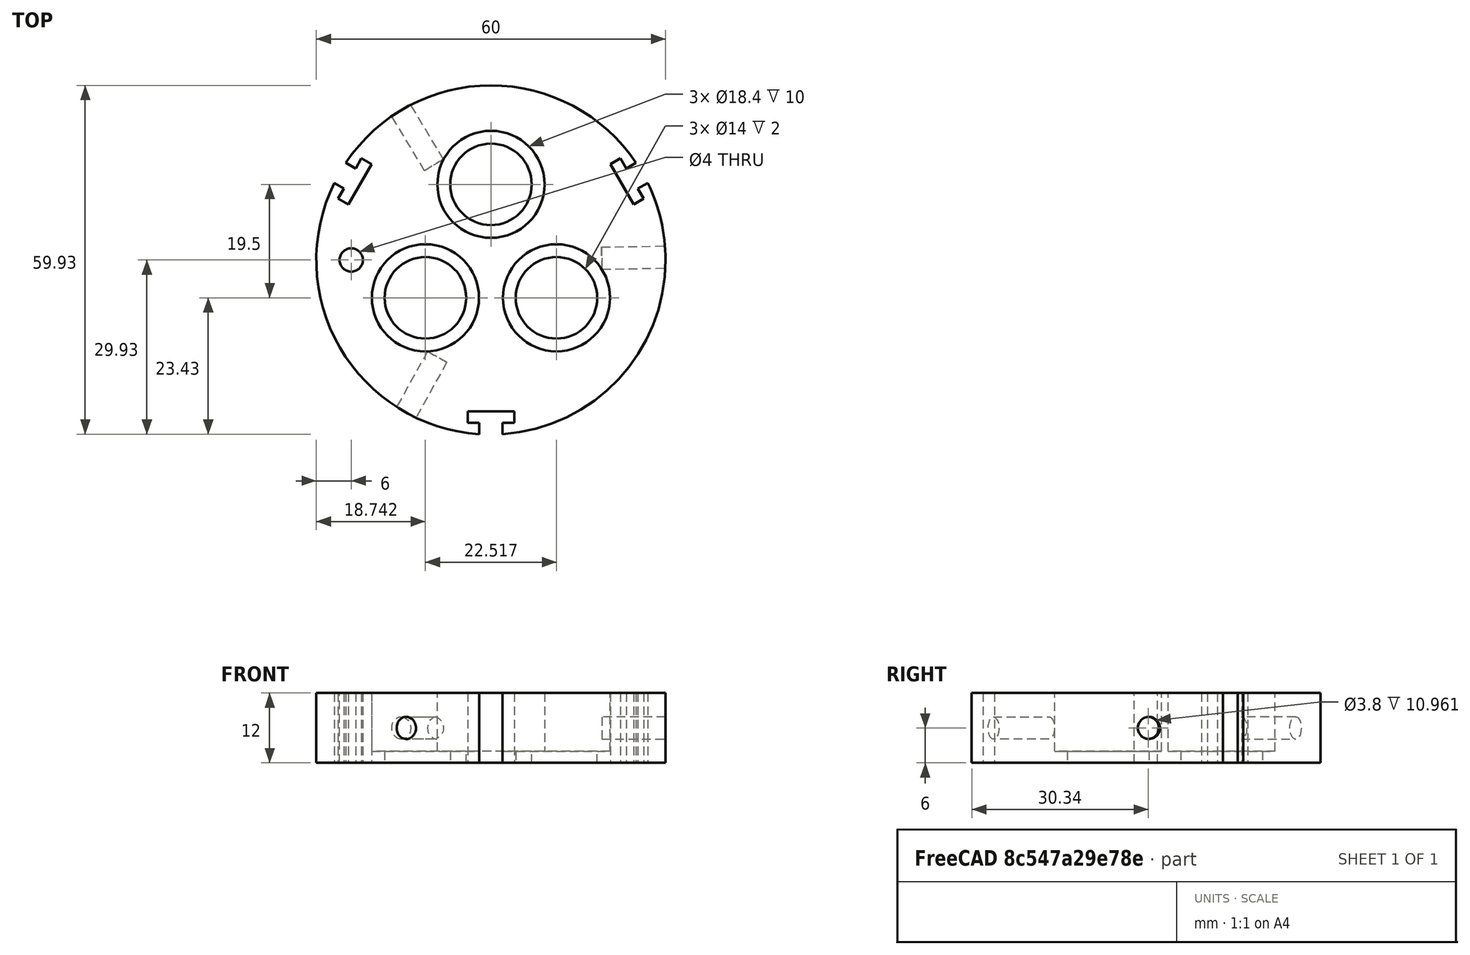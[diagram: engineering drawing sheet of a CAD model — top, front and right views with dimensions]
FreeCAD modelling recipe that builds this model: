
FCSTD DOCUMENT  (FreeCAD 1.0R38641 +468 (Git))
Label: Support_mot_3aileronsT_haut_60
License: All rights reserved
LicenseURL: https://en.wikipedia.org/wiki/All_rights_reserved
objects: Sketcher::SketchObject×6, PartDesign::Pocket×4, PartDesign::PolarPattern×3, PartDesign::Pad×2, PartDesign::Plane×1, PartDesign::Body×1, Mesh::Feature×1
note: 38 computed .brp shape members not serialized (recipe doc carries the construction recipe); baked Part::Feature solids carry a one-line shape summary decoded from their .brp

FEATURE [Sketcher::SketchObject] Sketch
  ArcFitTolerance = 1e-06
  AttachmentSupport = -> [XY_Plane]
  FullyConstrained = true
  MakeInternals = false
  MapMode = 5
  sketch-geometry (1):
    g0: Circle CenterX=0 CenterY=0 CenterZ=0 NormalX=0 NormalY=0 NormalZ=1 AngleXU=0 Radius=30
  constraints (2):
    c: Diameter(g0) = 60
    c: Coincident(g0,g-1)
FEATURE [PartDesign::Pad] Pad
  Direction = (0,0,1)
  Length = 12
  Length2 = 10
  Profile = -> Sketch
  ReferenceAxis = -> Sketch [N_Axis]
  Refine = true
  Suppressed = false
  Type = 0
FEATURE [Sketcher::SketchObject] Sketch001
  ArcFitTolerance = 1e-06
  AttachmentSupport = -> [Pad]
  FullyConstrained = true
  MakeInternals = false
  MapMode = 5
  Placement = pos=(0,0,12) rot=(0,0,1;0rad)
  sketch-geometry (1):
    g0: Circle CenterX=0 CenterY=13 CenterZ=0 NormalX=0 NormalY=0 NormalZ=1 AngleXU=0 Radius=9.2
  constraints (3):
    c: Diameter(g0) = 18.4
    c: PointOnObject(g0,g-2)
    c: DistanceY(g-1,g0) = 13
FEATURE [PartDesign::Pocket] Pocket
  BaseFeature = -> Pad
  Direction = (0,0,-1)
  Length = 5
  Length2 = 5
  Profile = -> Sketch001
  ReferenceAxis = -> Sketch001 [N_Axis]
  Refine = true
  Suppressed = false
  Type = 1
FEATURE [PartDesign::PolarPattern] PolarPattern
  Angle = 360
  Axis = -> Sketch001 [N_Axis]
  BaseFeature = -> Pocket
  Mode = 0
  Occurrences = 3
  Offset = 120
  Originals = -> [Pocket]
  Refine = true
  Suppressed = false
  TransformMode = 0
FEATURE [Sketcher::SketchObject] Sketch003
  ArcFitTolerance = 1e-06
  FullyConstrained = true
  MakeInternals = false
  MapMode = 5
  Placement = pos=(0,0,12) rot=(0,0,1;0rad)
  sketch-geometry (8):
    g0: LineSegment StartX=-2 StartY=-28 StartZ=0 EndX=-2 EndY=-32 EndZ=0
    g1: LineSegment StartX=-2 StartY=-32 StartZ=0 EndX=2 EndY=-32 EndZ=0
    g2: LineSegment StartX=2 StartY=-32 StartZ=0 EndX=2 EndY=-28 EndZ=0
    g3: LineSegment StartX=2 StartY=-28 StartZ=0 EndX=-2 EndY=-28 EndZ=0
    g4: LineSegment StartX=-4 StartY=-26 StartZ=0 EndX=-4 EndY=-28 EndZ=0
    g5: LineSegment StartX=-4 StartY=-28 StartZ=0 EndX=4 EndY=-28 EndZ=0
    g6: LineSegment StartX=4 StartY=-28 StartZ=0 EndX=4 EndY=-26 EndZ=0
    g7: LineSegment StartX=4 StartY=-26 StartZ=0 EndX=-4 EndY=-26 EndZ=0
  constraints (24):
    c: Coincident(g0,g1)
    c: Coincident(g1,g2)
    c: Coincident(g2,g3)
    c: Coincident(g3,g0)
    c: Vertical(g0)
    c: Vertical(g2)
    c: Horizontal(g1)
    c: Horizontal(g3)
    c: Distance(g0,g2) = 4
    c: Distance(g1,g3) = 4
    c: DistanceX(g-1,g2) = 2
    c: DistanceY(g2,g-1) = 28
    c: Coincident(g4,g5)
    c: Coincident(g5,g6)
    c: Coincident(g6,g7)
    c: Coincident(g7,g4)
    c: Vertical(g4)
    c: Vertical(g6)
    c: Horizontal(g5)
    c: Horizontal(g7)
    c: PointOnObject(g2,g5)
    c: DistanceY(g6,g6) = 2
    c: DistanceX(g7,g7) = 8
    c: DistanceX(g2,g5) = 2
FEATURE [PartDesign::Pocket] Pocket002
  BaseFeature = -> PolarPattern
  Direction = (0,0,-1)
  Length = 5
  Length2 = 5
  Profile = -> Sketch003
  ReferenceAxis = -> Sketch003 [N_Axis]
  Refine = true
  Suppressed = false
  Type = 1
FEATURE [PartDesign::PolarPattern] PolarPattern001
  Angle = 360
  Axis = -> Sketch003 [N_Axis]
  BaseFeature = -> Pocket002
  Mode = 0
  Occurrences = 3
  Offset = 120
  Originals = -> [Pocket002]
  Refine = true
  Suppressed = false
  TransformMode = 0
FEATURE [PartDesign::Plane] DatumPlane
  Length = 62.8248
  MapMode = 45
  Placement = pos=(-14.9389,24.9036,6) rot=(-0.441996,-0.780563,-0.441996;1.81604rad)
  ResizeMode = 0
  Width = 95.0623
FEATURE [Sketcher::SketchObject] Sketch009
  ArcFitTolerance = 1e-06
  AttachmentSupport = -> [DatumPlane]
  FullyConstrained = true
  MakeInternals = false
  MapMode = 5
  Placement = pos=(-14.9389,24.9036,6) rot=(-0.441996,-0.780563,-0.441996;1.81604rad)
  sketch-geometry (1):
    g0: Circle CenterX=0 CenterY=0 CenterZ=0 NormalX=0 NormalY=0 NormalZ=1 AngleXU=0 Radius=1.9
  constraints (2):
    c: Diameter(g0) = 3.8
    c: Coincident(g0,g-1)
FEATURE [PartDesign::Pocket] Pocket004
  BaseFeature = -> PolarPattern001
  Direction = (0.514414,-0.857542,1e-16)
  Length = 20
  Length2 = 5
  Midplane = true
  Profile = -> Sketch009
  ReferenceAxis = -> Sketch009 [N_Axis]
  Refine = true
  Suppressed = false
  Type = 0
FEATURE [Sketcher::SketchObject] Sketch010
  ArcFitTolerance = 1e-06
  AttachmentSupport = -> [Pocket004]
  ExternalGeometry = -> [Pocket004]
  FullyConstrained = true
  MakeInternals = false
  MapMode = 5
  Placement = pos=(0,0,0) rot=(1,0,0;3.14159rad)
  sketch-geometry (6):
    g0: Circle CenterX=-11.2583 CenterY=6.5 CenterZ=0 NormalX=0 NormalY=0 NormalZ=1 AngleXU=0 Radius=9.2
    g1: Circle CenterX=11.2583 CenterY=6.5 CenterZ=0 NormalX=0 NormalY=0 NormalZ=1 AngleXU=0 Radius=9.2
    g2: Circle CenterX=0 CenterY=-13 CenterZ=0 NormalX=0 NormalY=0 NormalZ=1 AngleXU=0 Radius=9.2
    g3: Circle CenterX=-11.2583 CenterY=6.5 CenterZ=0 NormalX=0 NormalY=0 NormalZ=1 AngleXU=0 Radius=7
    g4: Circle CenterX=11.2583 CenterY=6.5 CenterZ=0 NormalX=0 NormalY=0 NormalZ=1 AngleXU=0 Radius=7
    g5: Circle CenterX=0 CenterY=-13 CenterZ=0 NormalX=0 NormalY=0 NormalZ=1 AngleXU=0 Radius=7
  constraints (12):
    c: Diameter(g0) = 18.4
    c: Coincident(g0,g-3)
    c: Coincident(g1,g-4)
    c: Equal(g1,g-4)
    c: Coincident(g2,g-5)
    c: Equal(g2,g-5)
    c: Diameter(g3) = 14
    c: Coincident(g3,g0)
    c: Diameter(g4) = 14
    c: Coincident(g4,g1)
    c: Diameter(g5) = 14
    c: Coincident(g5,g2)
FEATURE [PartDesign::Pad] Pad001
  BaseFeature = -> Pocket004
  Direction = (0,0,-1)
  Length = 2
  Length2 = 10
  Profile = -> Sketch010
  ReferenceAxis = -> Sketch010 [N_Axis]
  Refine = true
  Reversed = true
  Suppressed = false
  Type = 0
FEATURE [Sketcher::SketchObject] Sketch011
  ArcFitTolerance = 1e-06
  AttachmentSupport = -> [Pad001]
  FullyConstrained = true
  MakeInternals = false
  MapMode = 5
  Placement = pos=(0,0,12) rot=(0,0,1;0rad)
  sketch-geometry (1):
    g0: Circle CenterX=-24 CenterY=0 CenterZ=0 NormalX=0 NormalY=0 NormalZ=1 AngleXU=0 Radius=2
  constraints (3):
    c: Diameter(g0) = 4
    c: PointOnObject(g0,g-1)
    c: DistanceX(g0,g-1) = 24
FEATURE [PartDesign::Pocket] Pocket005
  BaseFeature = -> Pad001
  Direction = (0,0,-1)
  Length = 5
  Length2 = 5
  Profile = -> Sketch011
  ReferenceAxis = -> Sketch011 [N_Axis]
  Refine = true
  Suppressed = false
  Type = 1
FEATURE [PartDesign::PolarPattern] PolarPattern002
  Angle = 360
  Axis = -> Z_Axis
  BaseFeature = -> Pocket005
  Mode = 0
  Occurrences = 3
  Offset = 120
  Originals = -> [Pocket004]
  Refine = true
  Suppressed = false
  TransformMode = 0
FEATURE [PartDesign::Body] Body  label="Corps"
  AllowCompound = false
  Group = -> [Sketch,Pad,Sketch001,Pocket,PolarPattern,Sketch003,Pocket002,PolarPattern001,DatumPlane,Sketch009,Pocket004,Sketch010,Pad001,Sketch011,Pocket005,PolarPattern002]
  Origin = -> Origin
  Tip = -> PolarPattern002
FEATURE [Mesh::Feature] Mesh  label="PolarPattern002 (Meshed)"
